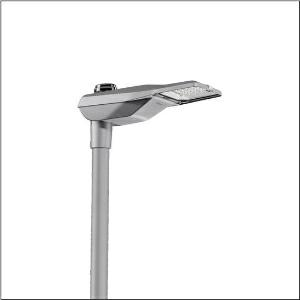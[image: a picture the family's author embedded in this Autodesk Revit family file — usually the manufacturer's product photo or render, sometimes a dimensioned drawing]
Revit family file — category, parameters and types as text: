
# Revit family: streetlight_sl_21_micro___st1_5a_5xe5p47n08db_8f26
name_source: partatom
category: Lighting Fixtures
units: mm (PartAtom-declared; Revit-internal decimal feet)

## family parameters
Cut with Voids When Loaded = No
Host = Face
Light Source = No
Part Type = Normal
Room Calculation Point = No
Round Connector Dimension = Use Diameter
Shared = No

## types (1)
- --- (1 x LED, 5230 lm, 39.1 W, 4000K)
    Apparent Load = 39 VA
    CIE Flux Codes = 22 53 95 100 100
    Color Rendering = 70
    Color Temperature = 4000K
    Default Elevation = 1800 mm
    Description = Streetlight SL 21 micro, mast luminaire, primary light control with lens, of PMMA, primary optical cover: cover, of toughened safety glass, transparent, light distribution: ST1.5a, light emission: direct distribution, primary light characteristic: asymmetric, installation type: post-top, LED, 3G 1.5mm², High Power LED, rated luminous flux: 5.230lm, luminous efficacy: 134lm/W, light colour: 740, colour temperature: 4000K, control: overheat protection, presetting dimming linear, constant luminous flux control, time-dependent luminous flux control, flexible luminous flux parameterisation, mains connection: 230..240V, AC, 50/60Hz, connection cable pre-assembled, cable length: 6,5m, wiring characteristics: H07RN-F, start of lifetime: 39W, end of service life: 41W, reduction: 18W, luminaire housing, of diecast aluminium (EN AC-44300), powder-coated, Siteco® metallic grey (DB 702S), corrosivity category C5 mid according to DIN EN ISO 12944, multi-level sealing system, sealing non-destructively replaceable, inclination adjustable: 0°, 5°, 10°, 15°, length: 528mm, width: 235mm, height: 110mm, spigot size: 76/60mm (post-top), protection rating (complete): IP66, insulation class (complete): insulation class I (protective earthing), certification: CE, ENEC, ENEC+, VDE, impact resistance: IK09, permissible operating ambient temperature for outdoor applications: -40..+50°C, standard-compliant lighting for roads and squares, packaging unit: 1 piece

Light Distribution: ST1.5a
    Height = 110 mm
    Lamp = 1 x LED
    Lamp Light Flux = 5230 lm
    Lamp Power = 39.1 W
    Lamp count = 1
    Length = 528 mm
    Luminous efficacy = 134 lm/W
    Manufacturer = Siteco
    ModVariant = No
    Model = 5XE5P47N08DB
    Number of Poles = 1
    OnlyDefault = Yes
    Power Factor = 1
    Product Name = Streetlight SL 21 micro | ST1.5a
    Product group = mast luminaire | pylon top
    ProductGroupID = 6100
    Protection Class = Protection class I
    Protection Degree = IP 66
    RLX_Detail_Level = 1
    RLX_Emergency_Light_Flux = 0 lm
    RLX_Emergency_Type = 0
    RLX_Emergency_Type_DB = No
    RlxData = <blob elided: 102173 chars, md5=e8c29218>
    Socket = socket
    Standby Power = 0 W
    System Light Flux = 5230 lm
    System Power = 39 W
    Type Comments = factory setting: luminous flux: 100 % | dim-lin: 254 | 765 mA
    Type Image = l_1294375.jpg
    URL = http://relux.com
    VarID = @adj_083073
    Voltage = 0 V
    Weight = 0.00 kg
    Width = 235 mm

## geometry (parser evidence)
native form markers: Blend x4, Sweep x11
no freeform markers — native parametric forms only
